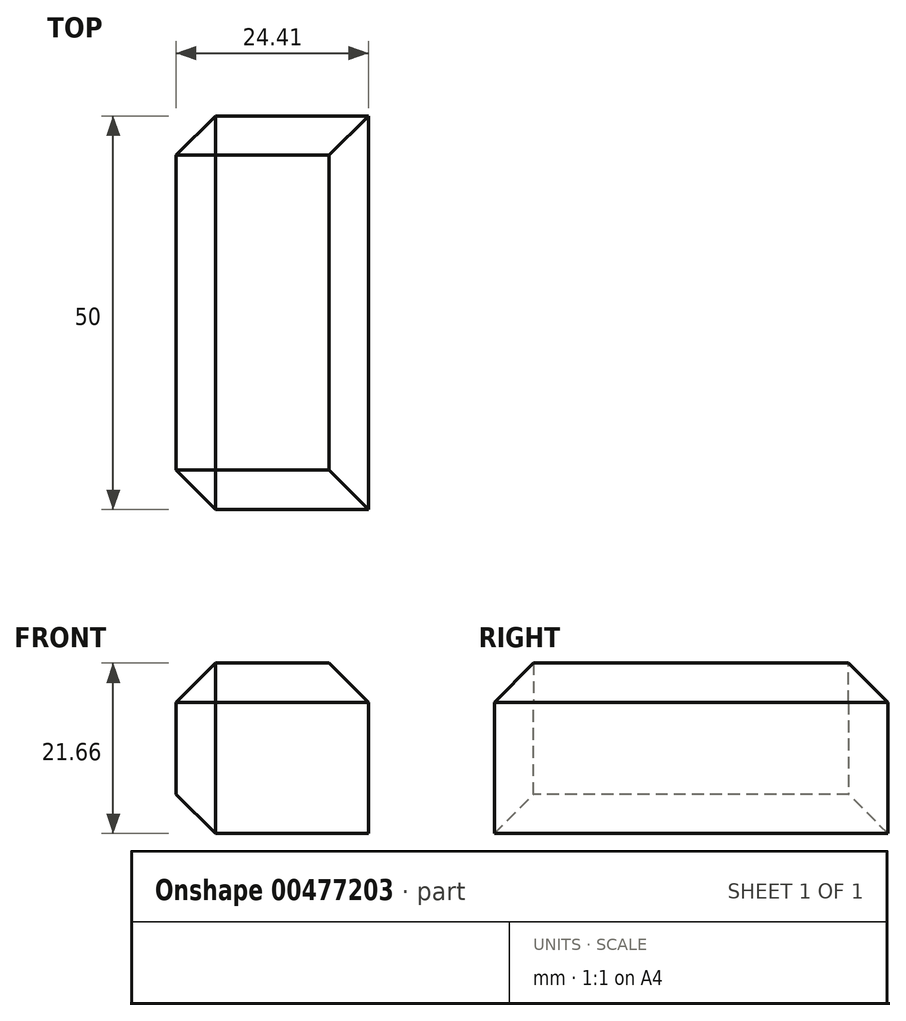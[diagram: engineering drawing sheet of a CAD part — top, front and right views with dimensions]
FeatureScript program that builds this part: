
annotation { "Feature Type Name" : "Feature", "Feature Type Description" : "" }
export const myFeature = defineFeature(function(context is Context, id is Id, definition is map)
    precondition{}
    {
        {
            var Q0;
            Q0=qCreatedBy(makeId("Front.planeOp"),FACE);
            var sketch = newSketch(context, id + "F0", { "sketchPlane" : qUnion([Q0])});
            skLineSegment(sketch, "E0.bottom", {"start": v(-63.34, 64.85) * mm, "end": v(-38.93, 64.85) * mm});
            skLineSegment(sketch, "E0.top", {"start": v(-63.34, 43.2) * mm, "end": v(-38.93, 43.2) * mm});
            skLineSegment(sketch, "E0.left", {"start": v(-63.34, 64.85) * mm, "end": v(-63.34, 43.2) * mm});
            skLineSegment(sketch, "E0.right", {"start": v(-38.93, 64.85) * mm, "end": v(-38.93, 43.2) * mm});
            skSolve(sketch);
        }
        {
            var Q0;
            Q0=makeQuery(id+"F0.imprint","IMPRINT",FACE,{"disambiguationData":[TD([[makeQuery(id+"F0.imprint","IMPRINT",EDGE,{"derivedFrom":sQuery(id+"F0.wireOp",EDGE,"E0.bottom")}),-1.0]])]});
            extrude(context, id + "F1", {"entities" : qUnion([Q0]), "depth" : 50 * mm});
        }
        {
            var Q0;
            Q0=makeQuery(id+"F1.opExtrude","SWEPT_FACE",FACE,{"disambiguationData":[OSD([sQuery(id+"F0.wireOp",EDGE,"E0.left")])]});
            var Q1;
            Q1=makeQuery(id+"F1.opExtrude","SWEPT_FACE",FACE,{"disambiguationData":[OSD([sQuery(id+"F0.wireOp",EDGE,"E0.bottom")])]});
            chamfer(context, id + "F2", {"entities" : qUnion([Q0, Q1]), "width" : 5 * mm, "tangentPropagation" : true});
        }
    });
